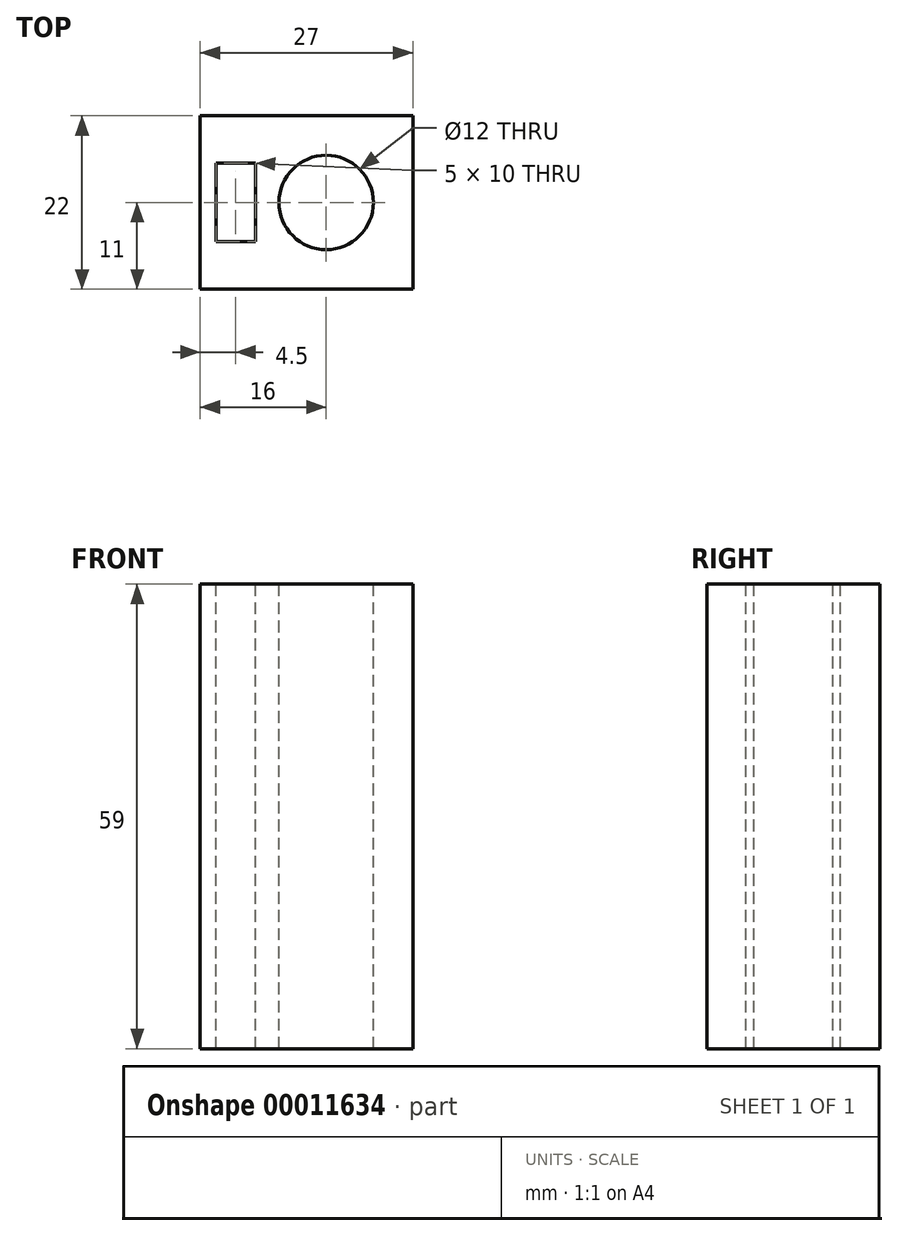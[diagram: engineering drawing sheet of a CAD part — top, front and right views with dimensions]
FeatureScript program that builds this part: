
annotation { "Feature Type Name" : "Feature", "Feature Type Description" : "" }
export const myFeature = defineFeature(function(context is Context, id is Id, definition is map)
    precondition{}
    {
        {
            var Q0;
            Q0=qCreatedBy(makeId("Top.planeOp"),FACE);
            var sketch = newSketch(context, id + "F0", { "sketchPlane" : qUnion([Q0])});
            skLineSegment(sketch, "E0.bottom", {"start": v(-13.5, 11) * mm, "end": v(13.5, 11) * mm});
            skLineSegment(sketch, "E0.top", {"start": v(-13.5, -11) * mm, "end": v(13.5, -11) * mm});
            skLineSegment(sketch, "E0.left", {"start": v(-13.5, 11) * mm, "end": v(-13.5, -11) * mm});
            skLineSegment(sketch, "E0.right", {"start": v(13.5, 11) * mm, "end": v(13.5, -11) * mm});
            skSolve(sketch);
        }
        {
            var Q0;
            Q0=makeQuery(id+"F0.imprint","IMPRINT",FACE,{"disambiguationData":[TD([[makeQuery(id+"F0.imprint","IMPRINT",EDGE,{"derivedFrom":sQuery(id+"F0.wireOp",EDGE,"E0.bottom")}),-1.0]])]});
            extrude(context, id + "F1", {"entities" : qUnion([Q0]), "depth" : (59 / 2) * mm, "hasSecondDirection" : true, "secondDirectionOppositeDirection" : true, "secondDirectionDepth" : 29.5 * mm});
        }
        {
            var Q0;
            Q0=makeQuery(id+"F1.opExtrude","CAP_FACE",FACE,{"disambiguationData":[OSD([sQuery(id+"F0.wireOp",EDGE,"E0.bottom"),sQuery(id+"F0.wireOp",EDGE,"E0.top"),sQuery(id+"F0.wireOp",EDGE,"E0.left"),sQuery(id+"F0.wireOp",EDGE,"E0.right")])],"isStart":false});
            var sketch = newSketch(context, id + "F2", { "sketchPlane" : qUnion([Q0])});
            skCircle(sketch, "E1", {"center": v(2.5, 0) * mm, "radius": 6 * mm});
            skSolve(sketch);
        }
        {
            var Q0;
            Q0 = qSketchRegion(id + "F2", true);
            extrude(context, id + "F3", {"entities" : qUnion([Q0]), "operationType" : NewBodyOperationType.REMOVE, "endBound" : BoundingType.UP_TO_NEXT, "oppositeDirection" : true, "depth" : 25 * mm});
        }
        {
            var Q0;
            Q0=makeQuery(id+"F1.opExtrude","CAP_FACE",FACE,{"disambiguationData":[OSD([sQuery(id+"F0.wireOp",EDGE,"E0.bottom"),sQuery(id+"F0.wireOp",EDGE,"E0.top"),sQuery(id+"F0.wireOp",EDGE,"E0.left"),sQuery(id+"F0.wireOp",EDGE,"E0.right")])],"isStart":false});
            var sketch = newSketch(context, id + "F4", { "sketchPlane" : qUnion([Q0])});
            skLineSegment(sketch, "E2.bottom", {"start": v(-6.5, 5) * mm, "end": v(-11.5, 5) * mm});
            skLineSegment(sketch, "E2.top", {"start": v(-6.5, -5) * mm, "end": v(-11.5, -5) * mm});
            skLineSegment(sketch, "E2.left", {"start": v(-6.5, 5) * mm, "end": v(-6.5, -5) * mm});
            skLineSegment(sketch, "E2.right", {"start": v(-11.5, 5) * mm, "end": v(-11.5, -5) * mm});
            skSolve(sketch);
        }
        {
            var Q0;
            Q0 = qSketchRegion(id + "F4", true);
            extrude(context, id + "F5", {"entities" : qUnion([Q0]), "operationType" : NewBodyOperationType.REMOVE, "endBound" : BoundingType.UP_TO_NEXT, "oppositeDirection" : true, "depth" : 25 * mm});
        }
    });
